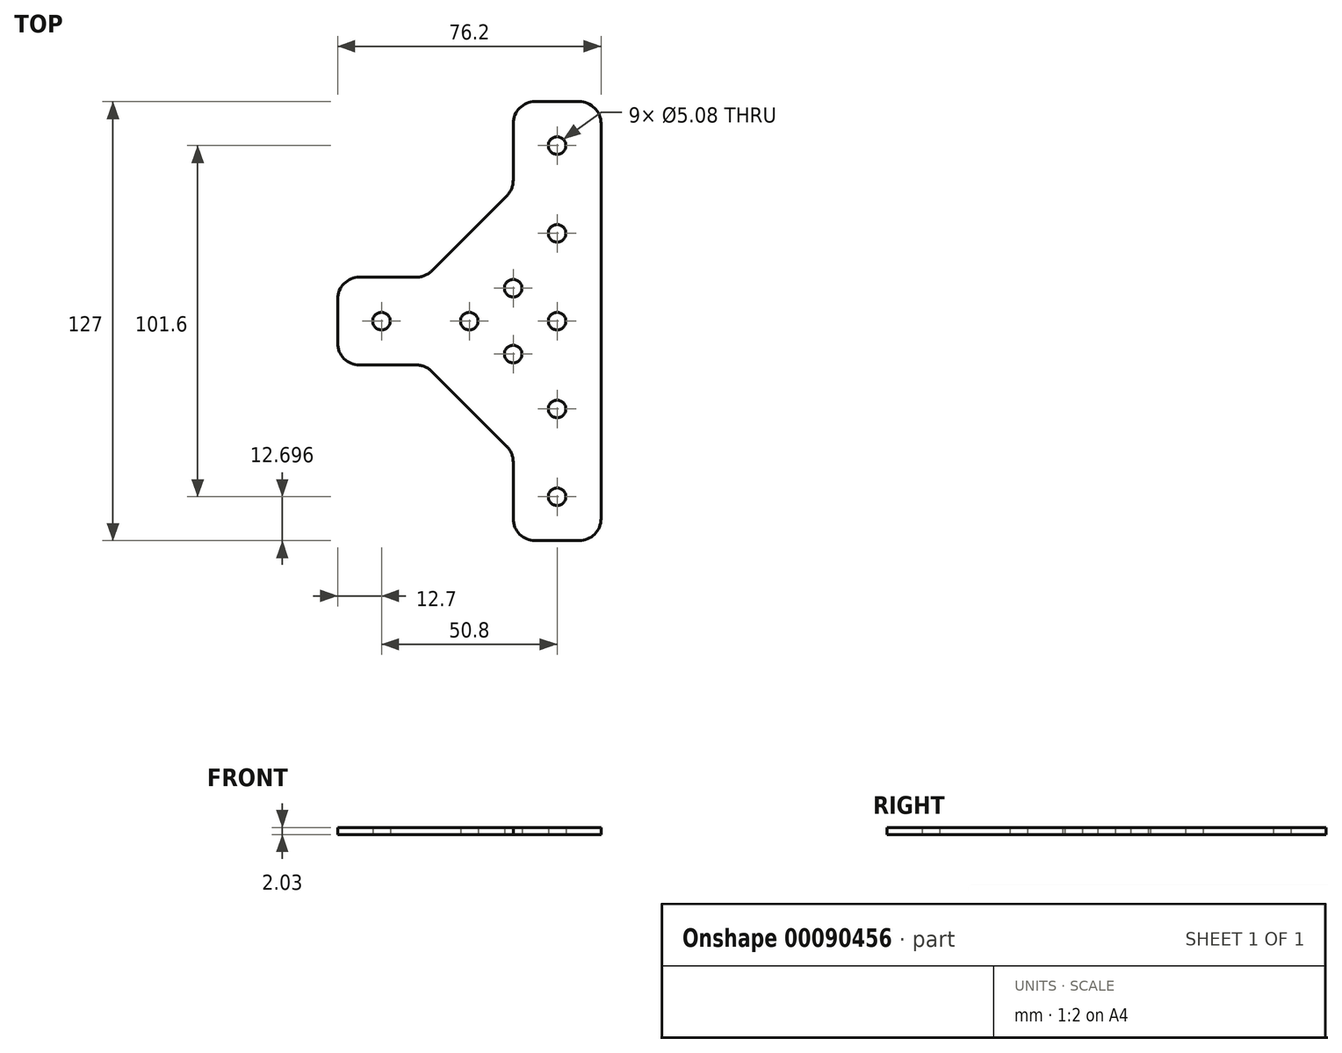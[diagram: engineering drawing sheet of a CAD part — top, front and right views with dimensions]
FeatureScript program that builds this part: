
annotation { "Feature Type Name" : "Feature", "Feature Type Description" : "" }
export const myFeature = defineFeature(function(context is Context, id is Id, definition is map)
    precondition{}
    {
        {
            var Q0;
            Q0=qCreatedBy(makeId("Top.planeOp"),FACE);
            var sketch = newSketch(context, id + "F0", { "sketchPlane" : qUnion([Q0])});
            skLineSegment(sketch, "E0", {"start": v(25.4, -71.35) * mm, "end": v(25.4, 42.95) * mm});
            skLineSegment(sketch, "E1", {"start": v(19.05, 49.3) * mm, "end": v(6.35, 49.3) * mm});
            skLineSegment(sketch, "E2", {"start": v(0, 42.95) * mm, "end": v(0, 26.53) * mm});
            skLineSegment(sketch, "E3", {"start": v(-1.86, 22.04) * mm, "end": v(-23.54, 0.36) * mm});
            skPoint(sketch, "E4.endSnap0", {"position": v(-15.24, -14.2) * mm});
            skLineSegment(sketch, "E5", {"start": v(-28.03, -1.5) * mm, "end": v(-44.45, -1.5) * mm});
            skLineSegment(sketch, "E6", {"start": v(-50.8, -7.85) * mm, "end": v(-50.8, -14.2) * mm});
            skLineSegment(sketch, "E7.MirrorCS", {"start": v(-50.8, -20.55) * mm, "end": v(-50.8, -14.2) * mm});
            skLineSegment(sketch, "E8.MirrorCS", {"start": v(-28.03, -26.9) * mm, "end": v(-44.45, -26.9) * mm});
            skLineSegment(sketch, "E9.MirrorCS", {"start": v(-1.86, -50.44) * mm, "end": v(-23.54, -28.76) * mm});
            skLineSegment(sketch, "E10.MirrorCS", {"start": v(0, -71.35) * mm, "end": v(0, -54.93) * mm});
            skLineSegment(sketch, "E11.MirrorCS", {"start": v(19.05, -77.7) * mm, "end": v(6.35, -77.7) * mm});
            skPoint(sketch, "E12.centerSnap0", {"position": v(12.7, -77.7) * mm});
            skLineSegment(sketch, "E13", {"start": v(12.7, -77.7) * mm, "end": v(12.7, -65) * mm});
            skCircle(sketch, "E14", {"center": v(12.7, -39.6) * mm, "radius": 2.54 * mm});
            skCircle(sketch, "E15", {"center": v(12.7, -65) * mm, "radius": 2.54 * mm});
            skCircle(sketch, "E16", {"center": v(12.7, -14.2) * mm, "radius": 2.54 * mm});
            skCircle(sketch, "E17", {"center": v(-38.1, -14.2) * mm, "radius": 2.54 * mm});
            skPoint(sketch, "E17.centerSnap0", {"position": v(-38.1, -1.5) * mm});
            skCircle(sketch, "E18", {"center": v(-12.7, -14.2) * mm, "radius": 2.54 * mm});
            skPoint(sketch, "E19.startSnap0", {"position": v(0, -14.2) * mm});
            skCircle(sketch, "E20", {"center": v(0, -23.73) * mm, "radius": 2.54 * mm});
            skCircle(sketch, "E21", {"center": v(0, -4.68) * mm, "radius": 2.54 * mm});
            skCircle(sketch, "E22.MirrorC", {"center": v(12.7, 11.2) * mm, "radius": 2.54 * mm});
            skCircle(sketch, "E23.MirrorC", {"center": v(12.7, 36.6) * mm, "radius": 2.54 * mm});
            skPoint(sketch, "E24.visualSharp", {"position": v(0, 23.9) * mm});
            skArc(sketch, "E24.filletArc", {"start": v(-1.86, 22.04) * mm, "mid": v(-0.48, 24.1) * mm, "end": v(0, 26.53) * mm});
            skPoint(sketch, "E25.visualSharp", {"position": v(0, 49.3) * mm});
            skArc(sketch, "E25.filletArc", {"start": v(6.35, 49.3) * mm, "mid": v(1.86, 47.44) * mm, "end": v(0, 42.95) * mm});
            skPoint(sketch, "E26.visualSharp", {"position": v(-25.4, -1.5) * mm});
            skArc(sketch, "E26.filletArc", {"start": v(-28.03, -1.5) * mm, "mid": v(-25.6, -1.02) * mm, "end": v(-23.54, 0.36) * mm});
            skPoint(sketch, "E27.visualSharp", {"position": v(25.4, 49.3) * mm});
            skArc(sketch, "E27.filletArc", {"start": v(25.4, 42.95) * mm, "mid": v(23.54, 47.44) * mm, "end": v(19.05, 49.3) * mm});
            skPoint(sketch, "E28.visualSharp", {"position": v(25.4, -77.7) * mm});
            skArc(sketch, "E28.filletArc", {"start": v(19.05, -77.7) * mm, "mid": v(23.54, -75.84) * mm, "end": v(25.4, -71.35) * mm});
            skPoint(sketch, "E29.visualSharp", {"position": v(0, -77.7) * mm});
            skArc(sketch, "E29.filletArc", {"start": v(0, -71.35) * mm, "mid": v(1.86, -75.84) * mm, "end": v(6.35, -77.7) * mm});
            skPoint(sketch, "E30.visualSharp", {"position": v(0, -52.3) * mm});
            skArc(sketch, "E30.filletArc", {"start": v(0, -54.93) * mm, "mid": v(-0.48, -52.5) * mm, "end": v(-1.86, -50.44) * mm});
            skPoint(sketch, "E31.visualSharp", {"position": v(-25.4, -26.9) * mm});
            skArc(sketch, "E31.filletArc", {"start": v(-23.54, -28.76) * mm, "mid": v(-25.6, -27.39) * mm, "end": v(-28.03, -26.9) * mm});
            skPoint(sketch, "E32.visualSharp", {"position": v(-50.8, -26.9) * mm});
            skArc(sketch, "E32.filletArc", {"start": v(-50.8, -20.55) * mm, "mid": v(-48.94, -25.04) * mm, "end": v(-44.45, -26.9) * mm});
            skPoint(sketch, "E33.visualSharp", {"position": v(-50.8, -1.5) * mm});
            skArc(sketch, "E33.filletArc", {"start": v(-44.45, -1.5) * mm, "mid": v(-48.94, -3.36) * mm, "end": v(-50.8, -7.85) * mm});
            skSolve(sketch);
        }
        {
            var Q0;
            Q0=makeQuery(id+"F0.imprint","IMPRINT",FACE,{"disambiguationData":[TD([[makeQuery(id+"F0.imprint","IMPRINT",EDGE,{"derivedFrom":sQuery(id+"F0.wireOp",EDGE,"E0")}),1.0]])]});
            extrude(context, id + "F1", {"entities" : qUnion([Q0]), "depth" : 2.03 * mm});
        }
    });
